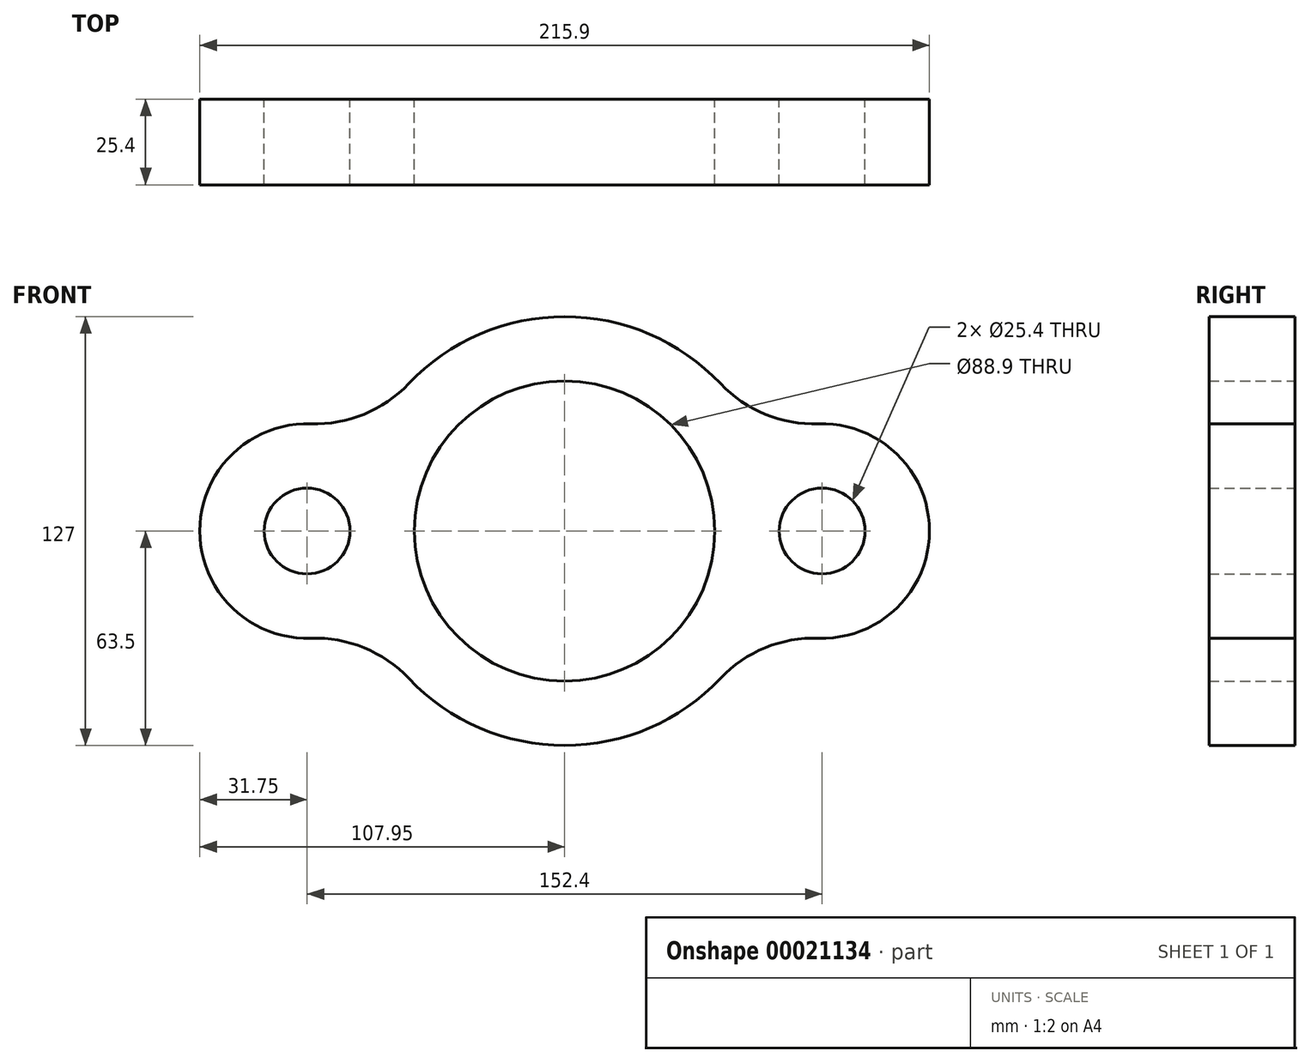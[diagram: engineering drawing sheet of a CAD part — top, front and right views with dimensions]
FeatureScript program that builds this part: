
annotation { "Feature Type Name" : "Feature", "Feature Type Description" : "" }
export const myFeature = defineFeature(function(context is Context, id is Id, definition is map)
    precondition{}
    {
        {
            var Q0;
            Q0=qCreatedBy(makeId("Front.planeOp"),FACE);
            var sketch = newSketch(context, id + "F0", { "sketchPlane" : qUnion([Q0])});
            skCircle(sketch, "E0", {"center": v(0, 0) * mm, "radius": 63.5 * mm});
            skCircle(sketch, "E1", {"center": v(-76.2, 0) * mm, "radius": 31.75 * mm});
            skCircle(sketch, "E2", {"center": v(76.2, 0) * mm, "radius": 31.75 * mm});
            skArc(sketch, "E3", {"start": v(-75.12, 31.73) * mm, "mid": v(-59.35, 34.56) * mm, "end": v(-46.14, 43.63) * mm});
            skArc(sketch, "E4", {"start": v(-46.14, -43.63) * mm, "mid": v(-59.35, -34.56) * mm, "end": v(-75.12, -31.73) * mm});
            skArc(sketch, "E5", {"start": v(75.12, -31.73) * mm, "mid": v(59.35, -34.56) * mm, "end": v(46.14, -43.63) * mm});
            skArc(sketch, "E6", {"start": v(46.14, 43.63) * mm, "mid": v(59.35, 34.56) * mm, "end": v(75.12, 31.73) * mm});
            skCircle(sketch, "E7", {"center": v(0, 0) * mm, "radius": 44.45 * mm});
            skCircle(sketch, "E8", {"center": v(-76.2, 0) * mm, "radius": 12.7 * mm});
            skCircle(sketch, "E9", {"center": v(76.2, 0) * mm, "radius": 12.7 * mm});
            skSolve(sketch);
        }
        {
            var Q0;
            {var subQ0=sQuery(id+"F0.wireOp",EDGE,"E8");Q0=makeQuery(id+"F0.imprint","IMPRINT",FACE,{"disambiguationData":[TD([[makeQuery(id+"F0.imprint","IMPRINT",EDGE,{"derivedFrom":subQ0}),-1.0]])]});}
            var Q1;
            {var subQ2=sQuery(id+"F0.wireOp",EDGE,"E0");var subQ5=makeQuery(id+"F0.imprint","INTERSECT",VERTEX,{"derivedFrom":[subQ2,sQuery(id+"F0.wireOp",EDGE,"E8")]});Q1=makeQuery(id+"F0.imprint","IMPRINT",FACE,{"disambiguationData":[TD([[makeQuery(id+"F0.imprint","IMPRINT",EDGE,{"disambiguationData":[TD([[subQ5,1.0]])],"derivedFrom":subQ2}),1.0]])]});}
            var Q2;
            {var subQ5=sQuery(id+"F0.wireOp",EDGE,"E0");var subQ9=makeQuery(id+"F0.imprint","INTERSECT",VERTEX,{"derivedFrom":[subQ5,sQuery(id+"F0.wireOp",EDGE,"E6")]});Q2=makeQuery(id+"F0.imprint","IMPRINT",FACE,{"disambiguationData":[TD([[makeQuery(id+"F0.imprint","IMPRINT",EDGE,{"disambiguationData":[TD([[subQ9,1.0]])],"derivedFrom":subQ5}),1.0]])]});}
            var Q3;
            {var subQ2=sQuery(id+"F0.wireOp",EDGE,"E0");var subQ5=makeQuery(id+"F0.imprint","INTERSECT",VERTEX,{"derivedFrom":[subQ2,sQuery(id+"F0.wireOp",EDGE,"E9")]});Q3=makeQuery(id+"F0.imprint","IMPRINT",FACE,{"disambiguationData":[TD([[makeQuery(id+"F0.imprint","IMPRINT",EDGE,{"disambiguationData":[TD([[subQ5,-1.0]])],"derivedFrom":subQ2}),1.0]])]});}
            var Q4;
            {var subQ5=sQuery(id+"F0.wireOp",EDGE,"E0");var subQ9=makeQuery(id+"F0.imprint","INTERSECT",VERTEX,{"derivedFrom":[subQ5,sQuery(id+"F0.wireOp",EDGE,"E4")]});Q4=makeQuery(id+"F0.imprint","IMPRINT",FACE,{"disambiguationData":[TD([[makeQuery(id+"F0.imprint","IMPRINT",EDGE,{"disambiguationData":[TD([[subQ9,1.0]])],"derivedFrom":subQ5}),1.0]])]});}
            var Q5;
            {var subQ3=sQuery(id+"F0.wireOp",EDGE,"E9");Q5=makeQuery(id+"F0.imprint","IMPRINT",FACE,{"disambiguationData":[TD([[makeQuery(id+"F0.imprint","IMPRINT",EDGE,{"derivedFrom":subQ3}),-1.0]])]});}
            var Q6;
            {var subQ0=sQuery(id+"F0.wireOp",EDGE,"E3");Q6=makeQuery(id+"F0.imprint","IMPRINT",FACE,{"disambiguationData":[TD([[makeQuery(id+"F0.imprint","IMPRINT",EDGE,{"derivedFrom":subQ0}),-1.0]])]});}
            var Q7;
            {var subQ0=sQuery(id+"F0.wireOp",EDGE,"E4");Q7=makeQuery(id+"F0.imprint","IMPRINT",FACE,{"disambiguationData":[TD([[makeQuery(id+"F0.imprint","IMPRINT",EDGE,{"derivedFrom":subQ0}),-1.0]])]});}
            var Q8;
            {var subQ3=sQuery(id+"F0.wireOp",EDGE,"E5");Q8=makeQuery(id+"F0.imprint","IMPRINT",FACE,{"disambiguationData":[TD([[makeQuery(id+"F0.imprint","IMPRINT",EDGE,{"derivedFrom":subQ3}),-1.0]])]});}
            var Q9;
            {var subQ0=sQuery(id+"F0.wireOp",EDGE,"E6");Q9=makeQuery(id+"F0.imprint","IMPRINT",FACE,{"disambiguationData":[TD([[makeQuery(id+"F0.imprint","IMPRINT",EDGE,{"derivedFrom":subQ0}),-1.0]])]});}
            extrude(context, id + "F1", {"entities" : qUnion([Q0, Q1, Q2, Q3, Q4, Q5, Q6, Q7, Q8, Q9]), "depth" : 25.4 * mm});
        }
    });
